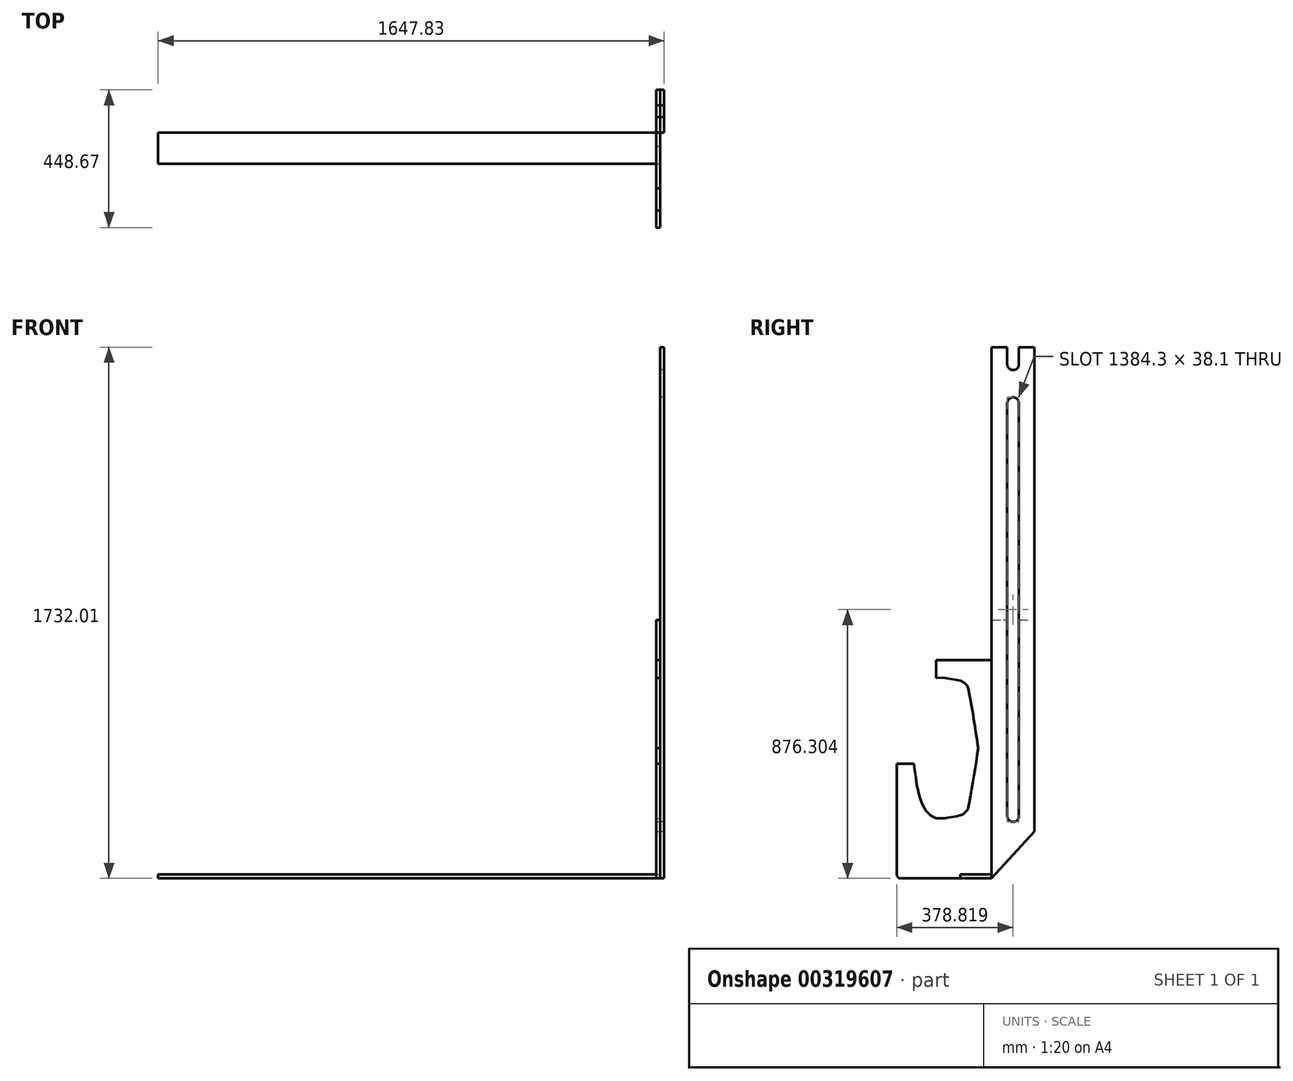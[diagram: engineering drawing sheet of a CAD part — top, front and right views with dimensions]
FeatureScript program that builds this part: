
annotation { "Feature Type Name" : "Feature", "Feature Type Description" : "" }
export const myFeature = defineFeature(function(context is Context, id is Id, definition is map)
    precondition{}
    {
        {
            var Q0;
            Q0=qCreatedBy(makeId("Right.planeOp"),FACE);
            cPlane(context, id + "F0", {"entities" : qUnion([Q0]), "cplaneType" : CPlaneType.OFFSET, "offset" : 304.8 * mm, "width" : 152.4 * mm, "height" : 152.4 * mm});
        }
        {
            var Q0;
            Q0=qCreatedBy(id+"F0.planeOp",FACE);
            var sketch = newSketch(context, id + "F1", { "sketchPlane" : qUnion([Q0])});
            skLineSegment(sketch, "E0", {"start": v(43.73, 367.26) * mm, "end": v(43.73, -475.75) * mm});
            skLineSegment(sketch, "E1", {"start": v(-265.24, -475.75) * mm, "end": v(-57.87, -475.75) * mm});
            skLineSegment(sketch, "E2", {"start": v(-293.1, 367.26) * mm, "end": v(94.53, 367.26) * mm});
            skLineSegment(sketch, "E3", {"start": v(43.73, -323.35) * mm, "end": v(43.73, -475.75) * mm});
            skLineSegment(sketch, "E4", {"start": v(43.73, -323.35) * mm, "end": v(183.43, -323.35) * mm});
            skLineSegment(sketch, "E5", {"start": v(183.43, -323.35) * mm, "end": v(183.43, 1256.26) * mm});
            skLineSegment(sketch, "E6", {"start": v(183.43, 1256.26) * mm, "end": v(132.63, 1256.26) * mm});
            skLineSegment(sketch, "E7", {"start": v(43.73, 1256.26) * mm, "end": v(43.73, 367.26) * mm});
            skLineSegment(sketch, "E8", {"start": v(113.58, -323.35) * mm, "end": v(113.58, -272.55) * mm});
            skLineSegment(sketch, "E9", {"start": v(113.58, -272.55) * mm, "end": v(113.58, 1073.65) * mm, "construction": true});
            skLineSegment(sketch, "E10", {"start": v(113.58, 1073.65) * mm, "end": v(113.58, 1200.65) * mm});
            skLineSegment(sketch, "E11", {"start": v(113.58, 1200.65) * mm, "end": v(113.58, 1256.26) * mm});
            skArc(sketch, "E12.0.startCap", {"start": v(132.63, 1200.65) * mm, "mid": v(113.58, 1181.6) * mm, "end": v(94.53, 1200.65) * mm});
            skLineSegment(sketch, "E12.0.left", {"start": v(94.53, 1200.65) * mm, "end": v(94.53, 1256.26) * mm});
            skLineSegment(sketch, "E12.0.right", {"start": v(132.63, 1200.65) * mm, "end": v(132.63, 1256.26) * mm});
            skLineSegment(sketch, "E13.trimOffspring", {"start": v(94.53, 1256.26) * mm, "end": v(43.73, 1256.26) * mm});
            skLineSegment(sketch, "E14", {"start": v(43.73, -475.75) * mm, "end": v(183.43, -323.35) * mm});
            skArc(sketch, "E15.0.startCap", {"start": v(132.63, -272.55) * mm, "mid": v(113.58, -291.6) * mm, "end": v(94.53, -272.55) * mm});
            skArc(sketch, "E15.0.endCap", {"start": v(94.53, 1073.65) * mm, "mid": v(113.58, 1092.7) * mm, "end": v(132.63, 1073.65) * mm});
            skLineSegment(sketch, "E15.0.left", {"start": v(94.53, -272.55) * mm, "end": v(94.53, 1073.65) * mm});
            skLineSegment(sketch, "E15.0.right", {"start": v(132.63, -272.55) * mm, "end": v(132.63, 1073.65) * mm});
            skLineSegment(sketch, "E16.trimOffspring", {"start": v(132.63, 367.26) * mm, "end": v(183.43, 367.26) * mm});
            skLineSegment(sketch, "E17", {"start": v(-57.87, -463.05) * mm, "end": v(43.73, -463.05) * mm});
            skLineSegment(sketch, "E18", {"start": v(-57.87, -463.05) * mm, "end": v(-57.87, -475.75) * mm});
            skLineSegment(sketch, "E19", {"start": v(-57.87, -475.75) * mm, "end": v(43.73, -475.75) * mm});
            skPoint(sketch, "E20.0", {"position": v(0, 0) * mm});
            skLineSegment(sketch, "E21", {"start": v(0, 0) * mm, "end": v(0, -50.8) * mm, "construction": true});
            skLineSegment(sketch, "E22", {"start": v(0, -50.8) * mm, "end": v(-381, -50.8) * mm, "construction": true});
            skFitSpline(sketch, "E23", {"points": [v(-214.38, -50.8) * mm, v(-212.1, -25.4) * mm, v(-209.55, 0) * mm, v(-206.5, 25.4) * mm, v(-202.7, 50.8) * mm, v(-198.37, 76.2) * mm, v(-193.04, 101.6) * mm, v(-184.66, 127) * mm, v(-170.94, 152.4) * mm, v(-155.2, 169.67) * mm, v(-137.67, 177.8) * mm, v(-105.66, 177.8) * mm, v(-104.4, 177.55) * mm, v(-79, 173.23) * mm, v(-53.6, 167.13) * mm, v(-35.81, 152.4) * mm, v(-29.21, 127) * mm, v(-24.38, 101.6) * mm, v(-20.07, 76.2) * mm, v(-15.75, 50.8) * mm, v(-11.68, 25.4) * mm, v(-7.62, 0) * mm, v(-3.56, -25.4) * mm, v(0, -50.8) * mm], "startDerivative": vector(60.68, 1027.8) * mm, "endDerivative": vector(77.6, -575.97) * mm});
            skFitSpline(sketch, "E24.MirrorCS", {"points": [v(-214.38, -50.8) * mm, v(-212.1, -76.2) * mm, v(-209.55, -101.6) * mm, v(-206.5, -127) * mm, v(-202.7, -152.4) * mm, v(-198.37, -177.8) * mm, v(-193.04, -203.2) * mm, v(-184.66, -228.6) * mm, v(-170.94, -254) * mm, v(-155.2, -271.27) * mm, v(-137.67, -279.4) * mm, v(-105.66, -279.4) * mm, v(-104.4, -279.15) * mm, v(-79, -274.83) * mm, v(-53.6, -268.73) * mm, v(-35.81, -254) * mm, v(-29.21, -228.6) * mm, v(-24.38, -203.2) * mm, v(-20.07, -177.8) * mm, v(-15.75, -152.4) * mm, v(-11.68, -127) * mm, v(-7.62, -101.6) * mm, v(-3.56, -76.2) * mm, v(0, -50.8) * mm], "startDerivative": vector(60.68, -1027.8) * mm, "endDerivative": vector(77.6, 575.97) * mm});
            skLineSegment(sketch, "E25", {"start": v(-209.55, -101.6) * mm, "end": v(-265.24, -101.6) * mm});
            skLineSegment(sketch, "E26", {"start": v(-265.24, -101.6) * mm, "end": v(-265.24, -475.75) * mm});
            skLineSegment(sketch, "E27", {"start": v(-137.67, 177.8) * mm, "end": v(-137.67, 235.98) * mm});
            skLineSegment(sketch, "E28", {"start": v(-137.67, 235.98) * mm, "end": v(43.73, 235.98) * mm});
            skSolve(sketch);
        }
        {
            var Q0;
            {var subQ3=sQuery(id+"F1.wireOp",EDGE,"E0");var subQ5=makeQuery(id+"F1.imprint","INTERSECT",VERTEX,{"derivedFrom":[subQ3,sQuery(id+"F1.wireOp",EDGE,"E28")]});Q0=makeQuery(id+"F1.imprint","IMPRINT",FACE,{"disambiguationData":[TD([[makeQuery(id+"F1.imprint","IMPRINT",EDGE,{"disambiguationData":[TD([[subQ5,-1.0]])],"derivedFrom":subQ3}),1.0]])]});}
            var Q1;
            {var subQ5=sQuery(id+"F1.wireOp",EDGE,"E16.trimOffspring");Q1=makeQuery(id+"F1.imprint","IMPRINT",FACE,{"disambiguationData":[TD([[makeQuery(id+"F1.imprint","IMPRINT",EDGE,{"derivedFrom":subQ5}),-1.0]])]});}
            var Q2;
            {var subQ4=sQuery(id+"F1.wireOp",EDGE,"E14");Q2=makeQuery(id+"F1.imprint","IMPRINT",FACE,{"disambiguationData":[TD([[makeQuery(id+"F1.imprint","IMPRINT",EDGE,{"derivedFrom":subQ4}),1.0]])]});}
            var Q3;
            {var subQ10=sQuery(id+"F1.wireOp",EDGE,"E7");Q3=makeQuery(id+"F1.imprint","IMPRINT",FACE,{"disambiguationData":[TD([[makeQuery(id+"F1.imprint","IMPRINT",EDGE,{"derivedFrom":subQ10}),1.0]])]});}
            var Q4;
            {var subQ8=sQuery(id+"F1.wireOp",EDGE,"E6");Q4=makeQuery(id+"F1.imprint","IMPRINT",FACE,{"disambiguationData":[TD([[makeQuery(id+"F1.imprint","IMPRINT",EDGE,{"derivedFrom":subQ8}),1.0]])]});}
            extrude(context, id + "F2", {"entities" : qUnion([Q0, Q1, Q2, Q3, Q4]), "depth" : 12.7 * mm});
        }
        {
            var Q0;
            {var subQ3=sQuery(id+"F1.wireOp",EDGE,"E0");var subQ5=makeQuery(id+"F1.imprint","INTERSECT",VERTEX,{"derivedFrom":[subQ3,sQuery(id+"F1.wireOp",EDGE,"E28")]});Q0=makeQuery(id+"F1.imprint","IMPRINT",FACE,{"disambiguationData":[TD([[makeQuery(id+"F1.imprint","IMPRINT",EDGE,{"disambiguationData":[TD([[subQ5,-1.0]])],"derivedFrom":subQ3}),1.0]])]});}
            var Q1;
            {var subQ5=sQuery(id+"F1.wireOp",EDGE,"E16.trimOffspring");Q1=makeQuery(id+"F1.imprint","IMPRINT",FACE,{"disambiguationData":[TD([[makeQuery(id+"F1.imprint","IMPRINT",EDGE,{"derivedFrom":subQ5}),-1.0]])]});}
            var Q2;
            {var subQ4=sQuery(id+"F1.wireOp",EDGE,"E14");Q2=makeQuery(id+"F1.imprint","IMPRINT",FACE,{"disambiguationData":[TD([[makeQuery(id+"F1.imprint","IMPRINT",EDGE,{"derivedFrom":subQ4}),1.0]])]});}
            var Q3;
            Q3=makeQuery(id+"F1.imprint","IMPRINT",FACE,{"disambiguationData":[TD([[makeQuery(id+"F1.imprint","IMPRINT",EDGE,{"derivedFrom":sQuery(id+"F1.wireOp",EDGE,"E1")}),1.0]])]});
            extrude(context, id + "F3", {"entities" : qUnion([Q0, Q1, Q2, Q3]), "oppositeDirection" : true, "depth" : 12.7 * mm});
        }
        {
            var Q0;
            Q0=makeQuery(id+"F3.opExtrude","SWEPT_EDGE",EDGE,{"disambiguationData":[OSD([sQuery(id+"F1.wireOp",EDGE,"E1"),sQuery(id+"F1.wireOp",EDGE,"E26")])]});
            var Q1;
            Q1=makeQuery(id+"F3.opExtrude","SWEPT_EDGE",EDGE,{"disambiguationData":[OSD([sQuery(id+"F1.wireOp",EDGE,"coLAoSVr-Ia8D-gwG0-CF7y-Y9HTY6ap8dqx"),sQuery(id+"F1.wireOp",EDGE,"FIVnMDtO-gRdL-i8XS-K6Nn-A1GGm4IowgBj")])]});
            var Q2;
            Q2=makeQuery(id+"F3.opExtrude","SWEPT_EDGE",EDGE,{"disambiguationData":[OSD([sQuery(id+"F1.wireOp",EDGE,"ec041011-ae58-4d85-beb0-4e1282e2a504"),sQuery(id+"F1.wireOp",EDGE,"lfF5s2z0-FZdm-HdAL-mSkM-j5f3lWNMjaFL")])]});
            var Q3;
            Q3=makeQuery(id+"F3.opExtrude","SWEPT_EDGE",EDGE,{"disambiguationData":[OSD([sQuery(id+"F1.wireOp",EDGE,"E2"),sQuery(id+"F1.wireOp",EDGE,"E15.0.left")])]});
            fillet(context, id + "F4", {"entities" : qUnion([Q0, Q1, Q2, Q3]), "radius" : 12.7 * mm, "tangentPropagation" : true, "allowEdgeOverflow" : false});
        }
        {
            var Q0;
            {var subQ2=sQuery(id+"F1.wireOp",EDGE,"E17");Q0=makeQuery(id+"F1.imprint","IMPRINT",FACE,{"disambiguationData":[TD([[makeQuery(id+"F1.imprint","IMPRINT",EDGE,{"derivedFrom":subQ2}),-1.0]])]});}
            extrude(context, id + "F5", {"entities" : qUnion([Q0]), "oppositeDirection" : true, "depth" : 1635.12 * mm});
        }
    });
